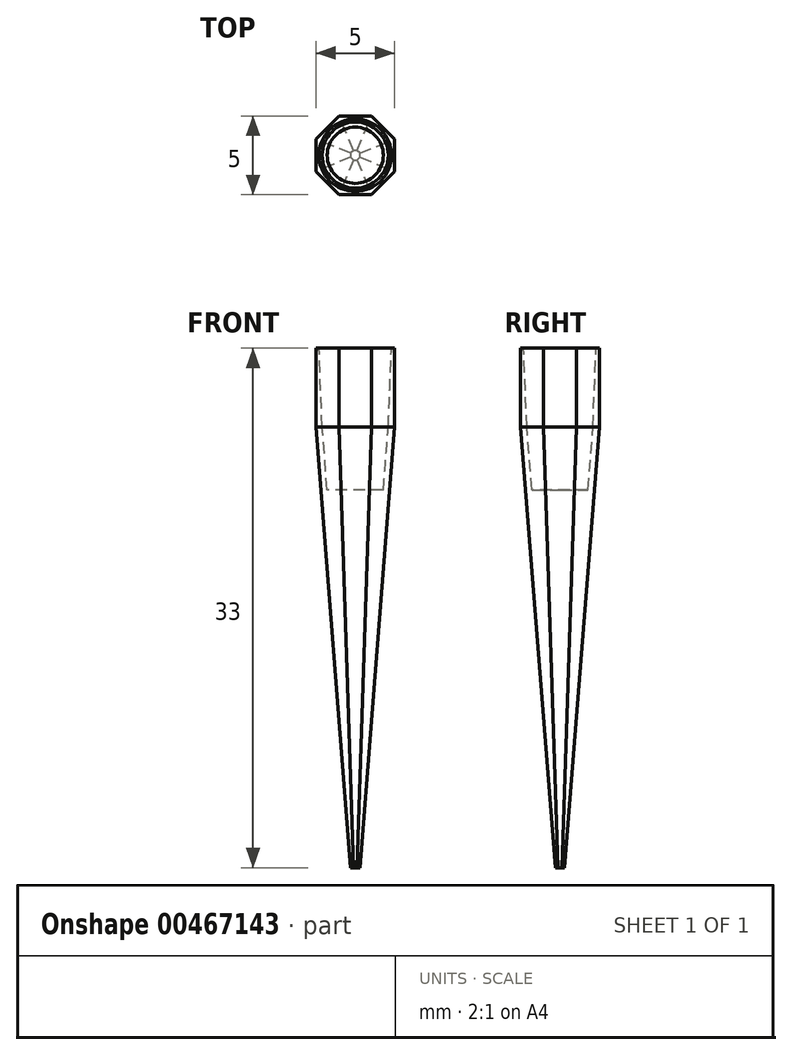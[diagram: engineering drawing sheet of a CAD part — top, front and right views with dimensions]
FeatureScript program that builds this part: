
annotation { "Feature Type Name" : "Feature", "Feature Type Description" : "" }
export const myFeature = defineFeature(function(context is Context, id is Id, definition is map)
    precondition{}
    {
        {
            var Q0;
            Q0=qCreatedBy(makeId("Right.planeOp"),FACE);
            var Q1;
            Q1=qCreatedBy(makeId("Front.planeOp"),FACE);
            cPlane(context, id + "F0", {"entities" : qUnion([Q0, Q1]), "cplaneType" : CPlaneType.MID_PLANE, "offset" : 25 * mm, "width" : 150 * mm, "height" : 150 * mm});
        }
        {
            var Q0;
            Q0=qCreatedBy(makeId("Top.planeOp"),FACE);
            cPlane(context, id + "F1", {"entities" : qUnion([Q0]), "cplaneType" : CPlaneType.OFFSET, "offset" : 2 * mm, "oppositeDirection" : true, "width" : 150 * mm, "height" : 150 * mm});
        }
        {
            var Q0;
            Q0=qCreatedBy(id+"F1.planeOp",FACE);
            cPlane(context, id + "F2", {"entities" : qUnion([Q0]), "cplaneType" : CPlaneType.OFFSET, "offset" : 2 * mm, "oppositeDirection" : true, "width" : 150 * mm, "height" : 150 * mm});
        }
        {
            var Q0;
            Q0=qCreatedBy(id+"F2.planeOp",FACE);
            cPlane(context, id + "F3", {"entities" : qUnion([Q0]), "cplaneType" : CPlaneType.OFFSET, "offset" : 3 * mm, "oppositeDirection" : true, "width" : 150 * mm, "height" : 150 * mm});
        }
        {
            var Q0;
            Q0=qCreatedBy(id+"F3.planeOp",FACE);
            cPlane(context, id + "F4", {"entities" : qUnion([Q0]), "cplaneType" : CPlaneType.OFFSET, "offset" : 4 * mm, "oppositeDirection" : true, "width" : 150 * mm, "height" : 150 * mm});
        }
        {
            var Q0;
            Q0=qCreatedBy(makeId("Top.planeOp"),FACE);
            var sketch = newSketch(context, id + "F5", { "sketchPlane" : qUnion([Q0])});
            skCircle(sketch, "E0", {"center": v(0, 0) * mm, "radius": 2.1 * mm});
            skCircle(sketch, "E1.cCircle", {"center": v(0, 0) * mm, "radius": 2.5 * mm, "construction": true});
            skLineSegment(sketch, "E1.0", {"start": v(2.5, 1.04) * mm, "end": v(2.5, -1.04) * mm});
            skLineSegment(sketch, "E1.1", {"start": v(2.5, -1.04) * mm, "end": v(1.04, -2.5) * mm});
            skLineSegment(sketch, "E1.2", {"start": v(1.04, -2.5) * mm, "end": v(-1.04, -2.5) * mm});
            skLineSegment(sketch, "E1.3", {"start": v(-1.04, -2.5) * mm, "end": v(-2.5, -1.04) * mm});
            skLineSegment(sketch, "E1.4", {"start": v(-2.5, -1.04) * mm, "end": v(-2.5, 1.04) * mm});
            skLineSegment(sketch, "E1.5", {"start": v(-2.5, 1.04) * mm, "end": v(-1.04, 2.5) * mm});
            skLineSegment(sketch, "E1.6", {"start": v(-1.04, 2.5) * mm, "end": v(1.04, 2.5) * mm});
            skLineSegment(sketch, "E1.7", {"start": v(1.04, 2.5) * mm, "end": v(2.5, 1.04) * mm});
            skPoint(sketch, "E1.0.midPoint", {"position": v(2.5, 0) * mm});
            skLineSegment(sketch, "E2", {"start": v(-1.04, -2.5) * mm, "end": v(-0.38, -2.1) * mm});
            skLineSegment(sketch, "E3", {"start": v(-0.38, -2.1) * mm, "end": v(0.38, -2.1) * mm});
            skLineSegment(sketch, "E4", {"start": v(0.38, -2.1) * mm, "end": v(1.04, -2.5) * mm});
            skSolve(sketch);
        }
        {
            var Q0;
            Q0=makeQuery(id+"F5.imprint","IMPRINT",FACE,{"disambiguationData":[TD([[makeQuery(id+"F5.imprint","IMPRINT",EDGE,{"derivedFrom":sQuery(id+"F5.wireOp",EDGE,"E0")}),1.0]])]});
            var Q1;
            Q1=makeQuery(id+"F5.imprint","IMPRINT",FACE,{"disambiguationData":[TD([[makeQuery(id+"F5.imprint","IMPRINT",EDGE,{"derivedFrom":sQuery(id+"F5.wireOp",EDGE,"Sb7no2BH-fZ8y-rcTk-OVMy-YQ3nKGef4sAo.bottom")}),1.0]])]});
            var Q2;
            {var subQ2=sQuery(id+"F5.wireOp",EDGE,"BvT99cy7-SZBb-MwwM-B7Nz-MiBXoH6qlrh5.bottom");Q2=makeQuery(id+"F5.imprint","IMPRINT",FACE,{"disambiguationData":[TD([[makeQuery(id+"F5.imprint","IMPRINT",EDGE,{"derivedFrom":subQ2}),-1.0]])]});}
            var Q3;
            {var subQ2=sQuery(id+"F5.wireOp",EDGE,"AdBRwbXI-zSZB-yZgz-3tIb-LB73Vqnebr5R.bottom");Q3=makeQuery(id+"F5.imprint","IMPRINT",FACE,{"disambiguationData":[TD([[makeQuery(id+"F5.imprint","IMPRINT",EDGE,{"derivedFrom":subQ2}),-1.0]])]});}
            var Q4;
            Q4=makeQuery(id+"F5.imprint","IMPRINT",FACE,{"disambiguationData":[TD([[makeQuery(id+"F5.imprint","IMPRINT",EDGE,{"derivedFrom":sQuery(id+"F5.wireOp",EDGE,"E1.0")}),-1.0]])]});
            var Q5;
            {var subQ5=sQuery(id+"F5.wireOp",EDGE,"E1.2");Q5=makeQuery(id+"F5.imprint","IMPRINT",FACE,{"disambiguationData":[TD([[makeQuery(id+"F5.imprint","IMPRINT",EDGE,{"derivedFrom":subQ5}),-1.0]])]});}
            extrude(context, id + "F6", {"entities" : qUnion([Q0, Q1, Q2, Q3, Q4, Q5]), "oppositeDirection" : true, "depth" : 28 * mm, "offsetDistance" : 25 * mm, "hasDraft" : true, "draftAngle" : 4.5 * degree, "draftPullDirection" : true});
        }
        {
            var Q0;
            Q0=makeQuery(id+"F5.imprint","IMPRINT",FACE,{"disambiguationData":[TD([[makeQuery(id+"F5.imprint","IMPRINT",EDGE,{"derivedFrom":sQuery(id+"F5.wireOp",EDGE,"E0")}),1.0]])]});
            extrude(context, id + "F7", {"entities" : qUnion([Q0]), "operationType" : NewBodyOperationType.REMOVE, "oppositeDirection" : true, "depth" : 4 * mm, "offsetDistance" : 25 * mm, "hasDraft" : true, "draftAngle" : 4.5 * degree, "draftPullDirection" : true});
        }
        {
            var Q0;
            {var subQ2=sQuery(id+"F5.wireOp",EDGE,"E0");Q0=makeQuery(id+"F5.imprint","IMPRINT",FACE,{"disambiguationData":[TD([[makeQuery(id+"F5.imprint","IMPRINT",EDGE,{"derivedFrom":subQ2}),-1.0]])]});}
            var Q1;
            Q1=makeQuery(id+"F5.imprint","IMPRINT",FACE,{"disambiguationData":[TD([[makeQuery(id+"F5.imprint","IMPRINT",EDGE,{"derivedFrom":sQuery(id+"F5.wireOp",EDGE,"E1.2")}),-1.0]])]});
            extrude(context, id + "F8", {"entities" : qUnion([Q0, Q1]), "operationType" : NewBodyOperationType.ADD, "depth" : 5 * mm, "offsetDistance" : 25 * mm});
        }
        {
            var Q0;
            Q0=makeQuery(id+"F8.opExtrude","CAP_EDGE",EDGE,{"disambiguationData":[OSD([sQuery(id+"F5.wireOp",EDGE,"E0")])],"isStart":false});
            chamfer(context, id + "F9", {"entities" : qUnion([Q0]), "chamferType" : ChamferType.TWO_OFFSETS, "width1" : 5 * mm, "oppositeDirection" : false, "width2" : 0.2 * mm, "tangentPropagation" : true});
        }
    });
